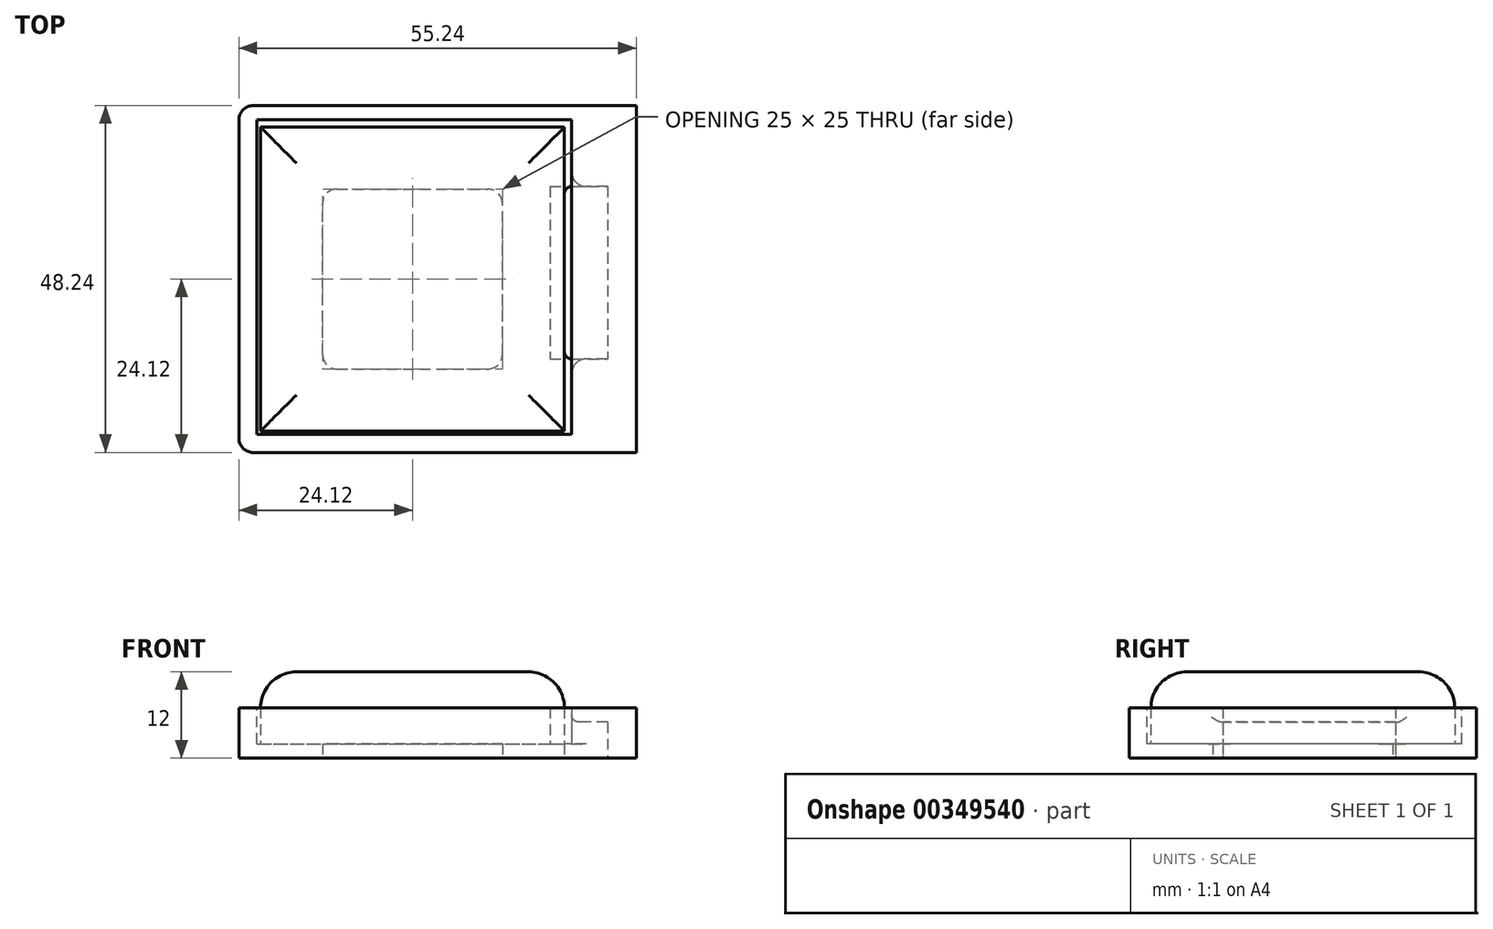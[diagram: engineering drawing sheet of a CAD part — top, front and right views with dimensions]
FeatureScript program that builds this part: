
annotation { "Feature Type Name" : "Feature", "Feature Type Description" : "" }
export const myFeature = defineFeature(function(context is Context, id is Id, definition is map)
    precondition{}
    {
        {
            var Q0;
            Q0=qCreatedBy(makeId("Top.planeOp"),FACE);
            var sketch = newSketch(context, id + "F0", { "sketchPlane" : qUnion([Q0])});
            skLineSegment(sketch, "E0.bottom", {"start": v(-21.12, 21.13) * mm, "end": v(21.13, 21.13) * mm});
            skLineSegment(sketch, "E0.top", {"start": v(-21.13, -21.12) * mm, "end": v(21.12, -21.12) * mm});
            skLineSegment(sketch, "E0.left", {"start": v(-21.12, 21.13) * mm, "end": v(-21.13, -21.12) * mm});
            skLineSegment(sketch, "E0.right", {"start": v(21.13, 21.13) * mm, "end": v(21.12, -21.12) * mm});
            skPoint(sketch, "E0.middle", {"position": v(0, 0) * mm});
            skSolve(sketch);
        }
        {
            var Q0;
            Q0 = qSketchRegion(id + "F0", true);
            extrude(context, id + "F1", {"entities" : qUnion([Q0]), "depth" : 10 * mm});
        }
        {
            var Q0;
            Q0=makeQuery(id+"F1.opExtrude","CAP_EDGE",EDGE,{"disambiguationData":[OSD([sQuery(id+"F0.wireOp",EDGE,"E0.left")])],"isStart":false});
            var Q1;
            Q1=makeQuery(id+"F1.opExtrude","CAP_EDGE",EDGE,{"disambiguationData":[OSD([sQuery(id+"F0.wireOp",EDGE,"E0.top")])],"isStart":false});
            var Q2;
            Q2=makeQuery(id+"F1.opExtrude","CAP_EDGE",EDGE,{"disambiguationData":[OSD([sQuery(id+"F0.wireOp",EDGE,"E0.right")])],"isStart":false});
            var Q3;
            Q3=makeQuery(id+"F1.opExtrude","CAP_EDGE",EDGE,{"disambiguationData":[OSD([sQuery(id+"F0.wireOp",EDGE,"E0.bottom")])],"isStart":false});
            fillet(context, id + "F2", {"entities" : qUnion([Q0, Q1, Q2, Q3]), "radius" : 5 * mm, "tangentPropagation" : true, "allowEdgeOverflow" : false});
        }
        {
            var Q0;
            Q0=makeQuery(id+"F1.opExtrude","SWEPT_FACE",FACE,{"disambiguationData":[OSD([sQuery(id+"F0.wireOp",EDGE,"E0.right")])]});
            var sketch = newSketch(context, id + "F3", { "sketchPlane" : qUnion([Q0])});
            skLineSegment(sketch, "E1.0", {"start": v(-21.12, 5) * mm, "end": v(-21.12, 0) * mm});
            skLineSegment(sketch, "E2.0", {"start": v(-11.12, 5) * mm, "end": v(-11.12, 0) * mm});
            skLineSegment(sketch, "E3.0", {"start": v(12.88, 5) * mm, "end": v(12.88, 0) * mm});
            skSolve(sketch);
        }
        {
            var Q0;
            Q0 = qSketchRegion(id + "F3", true);
            var Q1;
            {var subQ0=sQuery(id+"F3.wireOp",EDGE,"E2.0");Q1=makeQuery(id+"F3.imprint","IMPRINT",FACE,{"disambiguationData":[TD([[makeQuery(id+"F3.imprint","IMPRINT",EDGE,{"derivedFrom":subQ0}),1.0]])]});}
            extrude(context, id + "F4", {"entities" : qUnion([Q0, Q1]), "operationType" : NewBodyOperationType.REMOVE, "oppositeDirection" : true, "depth" : 2 * mm});
        }
        {
            var Q0;
            Q0=makeQuery(id+"F1.opExtrude","CAP_FACE",FACE,{"disambiguationData":[OSD([sQuery(id+"F0.wireOp",EDGE,"E0.bottom"),sQuery(id+"F0.wireOp",EDGE,"E0.top"),sQuery(id+"F0.wireOp",EDGE,"E0.left"),sQuery(id+"F0.wireOp",EDGE,"E0.right")])],"isStart":true});
            var sketch = newSketch(context, id + "F5", { "sketchPlane" : qUnion([Q0])});
            skLineSegment(sketch, "E4.0", {"start": v(-21.13, 21.12) * mm, "end": v(21.12, 21.12) * mm});
            skLineSegment(sketch, "E4.1", {"start": v(-21.12, -21.13) * mm, "end": v(21.13, -21.13) * mm});
            skLineSegment(sketch, "E4.2", {"start": v(21.13, -12.88) * mm, "end": v(21.12, 11.12) * mm});
            skLineSegment(sketch, "E4.3", {"start": v(21.12, 11.12) * mm, "end": v(21.12, 21.12) * mm});
            skLineSegment(sketch, "E4.4", {"start": v(21.13, -21.13) * mm, "end": v(21.13, -12.88) * mm});
            skLineSegment(sketch, "E5.0", {"start": v(-21.12, -21.13) * mm, "end": v(-21.13, 21.12) * mm});
            skLineSegment(sketch, "E6.0", {"start": v(19.13, -12.88) * mm, "end": v(21.13, -12.88) * mm});
            skLineSegment(sketch, "E6.1", {"start": v(19.12, 11.12) * mm, "end": v(21.12, 11.12) * mm});
            skLineSegment(sketch, "E7.0", {"start": v(22.13, -22.13) * mm, "end": v(22.13, -12.88) * mm});
            skLineSegment(sketch, "E7.1", {"start": v(22.13, 11.12) * mm, "end": v(22.12, 22.12) * mm});
            skLineSegment(sketch, "E7.2", {"start": v(-22.13, 22.12) * mm, "end": v(22.12, 22.12) * mm});
            skLineSegment(sketch, "E7.3", {"start": v(-22.12, -22.13) * mm, "end": v(-22.13, 22.12) * mm});
            skLineSegment(sketch, "E7.4", {"start": v(-22.12, -22.13) * mm, "end": v(22.13, -22.13) * mm});
            skLineSegment(sketch, "E8.0", {"start": v(24.13, -24.13) * mm, "end": v(24.13, -12.88) * mm});
            skLineSegment(sketch, "E8.1", {"start": v(24.12, 11.13) * mm, "end": v(24.12, 24.12) * mm});
            skLineSegment(sketch, "E8.2", {"start": v(-24.13, 24.12) * mm, "end": v(24.12, 24.12) * mm});
            skLineSegment(sketch, "E8.3", {"start": v(-24.12, -24.13) * mm, "end": v(-24.13, 24.12) * mm});
            skLineSegment(sketch, "E8.4", {"start": v(-24.12, -24.13) * mm, "end": v(24.13, -24.13) * mm});
            skLineSegment(sketch, "E9", {"start": v(24.13, -12.88) * mm, "end": v(22.13, -12.88) * mm});
            skLineSegment(sketch, "E10", {"start": v(24.12, 11.13) * mm, "end": v(22.13, 11.12) * mm});
            skSolve(sketch);
        }
        {
            var Q0;
            Q0=makeQuery(id+"F5.imprint","IMPRINT",FACE,{"disambiguationData":[TD([[makeQuery(id+"F5.imprint","IMPRINT",EDGE,{"derivedFrom":sQuery(id+"F5.wireOp",EDGE,"E4.0")}),-1.0]])]});
            var sketch = newSketch(context, id + "F6", { "sketchPlane" : qUnion([Q0])});
            skPoint(sketch, "E11.0", {"position": v(24.13, -24.13) * mm});
            skPoint(sketch, "E12.0", {"position": v(-24.13, 24.12) * mm});
            skLineSegment(sketch, "E13.bottom", {"start": v(24.13, -24.13) * mm, "end": v(-24.13, -24.13) * mm});
            skLineSegment(sketch, "E13.top", {"start": v(24.13, 24.12) * mm, "end": v(-24.13, 24.12) * mm});
            skLineSegment(sketch, "E13.left", {"start": v(24.13, -24.13) * mm, "end": v(24.13, 24.12) * mm});
            skLineSegment(sketch, "E13.right", {"start": v(-24.13, -24.13) * mm, "end": v(-24.13, 24.12) * mm});
            skSolve(sketch);
        }
        {
            var Q0;
            Q0 = qSketchRegion(id + "F6", true);
            extrude(context, id + "F7", {"entities" : qUnion([Q0]), "depth" : 2 * mm});
        }
        {
            var Q0;
            Q0=makeQuery(id+"F5.imprint","IMPRINT",FACE,{"disambiguationData":[TD([[makeQuery(id+"F5.imprint","IMPRINT",EDGE,{"derivedFrom":sQuery(id+"F5.wireOp",EDGE,"E7.0")}),-1.0]])]});
            extrude(context, id + "F8", {"entities" : qUnion([Q0]), "operationType" : NewBodyOperationType.ADD, "oppositeDirection" : true, "depth" : 5 * mm});
        }
        {
            var Q0;
            Q0=makeQuery(id+"F7.opExtrude","CAP_FACE",FACE,{"disambiguationData":[OSD([sQuery(id+"F6.wireOp",EDGE,"E13.bottom"),sQuery(id+"F6.wireOp",EDGE,"E13.top"),sQuery(id+"F6.wireOp",EDGE,"E13.left"),sQuery(id+"F6.wireOp",EDGE,"E13.right")])],"isStart":false});
            var sketch = newSketch(context, id + "F9", { "sketchPlane" : qUnion([Q0])});
            skLineSegment(sketch, "E14.0", {"start": v(21.13, -12.88) * mm, "end": v(21.12, 11.12) * mm});
            skLineSegment(sketch, "E15.0", {"start": v(19.13, -12.88) * mm, "end": v(24.13, -12.88) * mm});
            skLineSegment(sketch, "E16.0", {"start": v(19.13, 11.12) * mm, "end": v(24.13, 11.12) * mm});
            skLineSegment(sketch, "E17.0", {"start": v(24.13, -24.13) * mm, "end": v(24.13, 24.12) * mm});
            skSolve(sketch);
        }
        {
            var Q0;
            {var subQ0=sQuery(id+"F9.wireOp",EDGE,"E14.0");Q0=makeQuery(id+"F9.imprint","IMPRINT",FACE,{"disambiguationData":[TD([[makeQuery(id+"F9.imprint","IMPRINT",EDGE,{"derivedFrom":subQ0}),-1.0]])]});}
            extrude(context, id + "F10", {"entities" : qUnion([Q0]), "operationType" : NewBodyOperationType.REMOVE, "oppositeDirection" : true, "depth" : 25 * mm});
        }
        {
            var Q0;
            Q0=makeQuery(id+"F7.opExtrude","CAP_FACE",FACE,{"disambiguationData":[OSD([sQuery(id+"F6.wireOp",EDGE,"E13.bottom"),sQuery(id+"F6.wireOp",EDGE,"E13.top"),sQuery(id+"F6.wireOp",EDGE,"E13.left"),sQuery(id+"F6.wireOp",EDGE,"E13.right")])],"isStart":false});
            var sketch = newSketch(context, id + "F11", { "sketchPlane" : qUnion([Q0])});
            skLineSegment(sketch, "E18.0", {"start": v(21.12, 11.12) * mm, "end": v(24.13, 11.12) * mm});
            skLineSegment(sketch, "E19.0", {"start": v(21.13, -12.88) * mm, "end": v(21.12, 11.12) * mm});
            skLineSegment(sketch, "E20.0", {"start": v(21.13, -12.88) * mm, "end": v(24.13, -12.88) * mm});
            skLineSegment(sketch, "E21.0", {"start": v(24.13, 11.12) * mm, "end": v(24.13, 24.12) * mm});
            skLineSegment(sketch, "E22.0", {"start": v(24.13, 24.12) * mm, "end": v(-24.13, 24.12) * mm});
            skLineSegment(sketch, "E23.0", {"start": v(-24.13, -24.13) * mm, "end": v(-24.13, 24.12) * mm});
            skLineSegment(sketch, "E24.0", {"start": v(24.13, -24.13) * mm, "end": v(-24.13, -24.13) * mm});
            skLineSegment(sketch, "E25.0", {"start": v(24.13, -24.13) * mm, "end": v(24.13, -12.88) * mm});
            skLineSegment(sketch, "E26.MirrorCS", {"start": v(27.13, 11.12) * mm, "end": v(24.13, 11.12) * mm});
            skLineSegment(sketch, "E27.MirrorCS", {"start": v(27.13, -12.88) * mm, "end": v(27.13, 11.12) * mm});
            skLineSegment(sketch, "E28.MirrorCS", {"start": v(27.13, -12.88) * mm, "end": v(24.13, -12.88) * mm});
            skLineSegment(sketch, "E29.MirrorCS", {"start": v(24.13, -24.13) * mm, "end": v(72.38, -24.13) * mm});
            skLineSegment(sketch, "E30.MirrorCS", {"start": v(72.38, -24.13) * mm, "end": v(72.38, 24.12) * mm});
            skLineSegment(sketch, "E31.MirrorCS", {"start": v(24.13, 24.12) * mm, "end": v(72.38, 24.12) * mm});
            skLineSegment(sketch, "E32.0", {"start": v(15.13, -18.88) * mm, "end": v(24.13, -18.88) * mm});
            skLineSegment(sketch, "E32.1", {"start": v(15.12, 17.12) * mm, "end": v(24.13, 17.12) * mm});
            skLineSegment(sketch, "E32.2", {"start": v(33.13, 17.12) * mm, "end": v(24.13, 17.12) * mm});
            skLineSegment(sketch, "E32.3", {"start": v(15.13, -18.88) * mm, "end": v(15.12, 17.12) * mm});
            skLineSegment(sketch, "E32.4", {"start": v(33.13, -18.88) * mm, "end": v(33.13, 17.12) * mm});
            skLineSegment(sketch, "E32.5", {"start": v(33.13, -18.88) * mm, "end": v(24.13, -18.88) * mm});
            skLineSegment(sketch, "E33", {"start": v(24.13, 24.12) * mm, "end": v(24.13, -24.13) * mm});
            skLineSegment(sketch, "E34.MirrorCS", {"start": v(42.13, 24.12) * mm, "end": v(42.13, -24.13) * mm});
            skLineSegment(sketch, "E35.0", {"start": v(37.63, 24.12) * mm, "end": v(37.63, -24.13) * mm});
            skLineSegment(sketch, "E36.0", {"start": v(24.13, -14.13) * mm, "end": v(72.38, -14.13) * mm});
            skLineSegment(sketch, "E37.0", {"start": v(24.13, 14.12) * mm, "end": v(72.38, 14.12) * mm});
            skSolve(sketch);
        }
        {
            var Q0;
            {var subQ0=sQuery(id+"F11.wireOp",EDGE,"E32.2");Q0=makeQuery(id+"F11.imprint","IMPRINT",FACE,{"disambiguationData":[TD([[makeQuery(id+"F11.imprint","IMPRINT",EDGE,{"derivedFrom":subQ0}),-1.0]])]});}
            var Q1;
            {var subQ0=sQuery(id+"F11.wireOp",EDGE,"E34.MirrorCS");var subQ1=sQuery(id+"F11.wireOp",EDGE,"E31.MirrorCS");var subQ2=makeQuery(id+"F11.imprint","INTERSECT",VERTEX,{"derivedFrom":[subQ1,subQ0]});Q1=makeQuery(id+"F11.imprint","IMPRINT",FACE,{"disambiguationData":[TD([[makeQuery(id+"F11.imprint","IMPRINT",EDGE,{"disambiguationData":[TD([[subQ2,1.0]])],"derivedFrom":subQ1}),-1.0]])]});}
            var Q2;
            {var subQ0=sQuery(id+"F11.wireOp",EDGE,"E36.0");var subQ1=sQuery(id+"F11.wireOp",EDGE,"E32.4");var subQ2=makeQuery(id+"F11.imprint","INTERSECT",VERTEX,{"derivedFrom":[subQ1,subQ0]});Q2=makeQuery(id+"F11.imprint","IMPRINT",FACE,{"disambiguationData":[TD([[makeQuery(id+"F11.imprint","IMPRINT",EDGE,{"disambiguationData":[TD([[subQ2,-1.0]])],"derivedFrom":subQ1}),-1.0]])]});}
            var Q3;
            {var subQ0=sQuery(id+"F11.wireOp",EDGE,"E37.0");var subQ1=sQuery(id+"F11.wireOp",EDGE,"E34.MirrorCS");var subQ2=makeQuery(id+"F11.imprint","INTERSECT",VERTEX,{"derivedFrom":[subQ1,subQ0]});Q3=makeQuery(id+"F11.imprint","IMPRINT",FACE,{"disambiguationData":[TD([[makeQuery(id+"F11.imprint","IMPRINT",EDGE,{"disambiguationData":[TD([[subQ2,-1.0]])],"derivedFrom":subQ1}),-1.0]])]});}
            var Q4;
            {var subQ3=sQuery(id+"F11.wireOp",EDGE,"E32.5");Q4=makeQuery(id+"F11.imprint","IMPRINT",FACE,{"disambiguationData":[TD([[makeQuery(id+"F11.imprint","IMPRINT",EDGE,{"derivedFrom":subQ3}),1.0]])]});}
            var Q5;
            {var subQ0=sQuery(id+"F11.wireOp",EDGE,"E34.MirrorCS");var subQ1=sQuery(id+"F11.wireOp",EDGE,"E29.MirrorCS");var subQ2=makeQuery(id+"F11.imprint","INTERSECT",VERTEX,{"derivedFrom":[subQ1,subQ0]});Q5=makeQuery(id+"F11.imprint","IMPRINT",FACE,{"disambiguationData":[TD([[makeQuery(id+"F11.imprint","IMPRINT",EDGE,{"disambiguationData":[TD([[subQ2,1.0]])],"derivedFrom":subQ1}),1.0]])]});}
            var Q6;
            {var subQ7=sQuery(id+"F11.wireOp",EDGE,"E26.MirrorCS");Q6=makeQuery(id+"F11.imprint","IMPRINT",FACE,{"disambiguationData":[TD([[makeQuery(id+"F11.imprint","IMPRINT",EDGE,{"derivedFrom":subQ7}),-1.0]])]});}
            var Q7;
            {var subQ0=sQuery(id+"F11.wireOp",EDGE,"E32.5");Q7=makeQuery(id+"F11.imprint","IMPRINT",FACE,{"disambiguationData":[TD([[makeQuery(id+"F11.imprint","IMPRINT",EDGE,{"derivedFrom":subQ0}),-1.0]])]});}
            var Q8;
            {var subQ0=sQuery(id+"F11.wireOp",EDGE,"E32.2");Q8=makeQuery(id+"F11.imprint","IMPRINT",FACE,{"disambiguationData":[TD([[makeQuery(id+"F11.imprint","IMPRINT",EDGE,{"derivedFrom":subQ0}),1.0]])]});}
            extrude(context, id + "F12", {"entities" : qUnion([Q0, Q1, Q2, Q3, Q4, Q5, Q6, Q7, Q8]), "operationType" : NewBodyOperationType.ADD, "oppositeDirection" : true, "depth" : 4 * mm});
        }
        {
            var Q0;
            Q0=makeQuery(id+"F12.boolean.opBoolean","MERGE",FACE,{"derivedFrom":[makeQuery(id+"F8.boolean.opBoolean","MERGE",FACE,{"derivedFrom":[makeQuery(id+"F7.opExtrude","SWEPT_FACE",FACE,{"disambiguationData":[OSD([sQuery(id+"F6.wireOp",EDGE,"E13.top")])]}),makeQuery(id+"F8.opExtrude","SWEPT_FACE",FACE,{"disambiguationData":[OSD([sQuery(id+"F5.wireOp",EDGE,"E8.2")])]})]}),makeQuery(id+"F12.opExtrude","SWEPT_FACE",FACE,{"disambiguationData":[OSD([sQuery(id+"F11.wireOp",EDGE,"E31.MirrorCS")])]})]});
            var sketch = newSketch(context, id + "F13", { "sketchPlane" : qUnion([Q0])});
            skLineSegment(sketch, "E38.0", {"start": v(42.13, -2) * mm, "end": v(-24.13, -2) * mm});
            skLineSegment(sketch, "E39.0", {"start": v(-24.13, 5) * mm, "end": v(24.12, 5) * mm});
            skSolve(sketch);
        }
        {
            var Q0;
            Q0=makeQuery(id+"F12.opExtrude","CAP_FACE",FACE,{"disambiguationData":[OSD([sQuery(id+"F11.wireOp",EDGE,"E29.MirrorCS"),sQuery(id+"F11.wireOp",EDGE,"E31.MirrorCS"),sQuery(id+"F11.wireOp",EDGE,"E32.2"),sQuery(id+"F11.wireOp",EDGE,"E32.4"),sQuery(id+"F11.wireOp",EDGE,"E32.5"),sQuery(id+"F11.wireOp",EDGE,"E33"),sQuery(id+"F11.wireOp",EDGE,"E34.MirrorCS")])],"isStart":false});
            cPlane(context, id + "F14", {"entities" : qUnion([Q0]), "cplaneType" : CPlaneType.OFFSET, "offset" : 1 * mm, "width" : 150 * mm, "height" : 150 * mm});
        }
        {
            var Q0;
            Q0=qCreatedBy(id+"F14.planeOp",FACE);
            var sketch = newSketch(context, id + "F15", { "sketchPlane" : qUnion([Q0])});
            skLineSegment(sketch, "E40.0.0", {"start": v(42.13, -24.12) * mm, "end": v(42.13, 24.13) * mm});
            skLineSegment(sketch, "E40.0.1", {"start": v(42.13, 24.13) * mm, "end": v(24.13, 24.13) * mm});
            skLineSegment(sketch, "E40.0.2", {"start": v(24.13, 24.13) * mm, "end": v(24.13, 12.88) * mm});
            skLineSegment(sketch, "E40.0.3", {"start": v(24.13, 12.88) * mm, "end": v(27.13, 12.88) * mm});
            skLineSegment(sketch, "E40.0.4", {"start": v(27.13, 12.88) * mm, "end": v(27.13, -11.12) * mm});
            skLineSegment(sketch, "E40.0.5", {"start": v(27.13, -11.12) * mm, "end": v(24.12, -11.12) * mm});
            skLineSegment(sketch, "E40.0.6", {"start": v(24.13, -11.13) * mm, "end": v(24.13, -24.12) * mm});
            skLineSegment(sketch, "E40.0.7", {"start": v(24.13, -24.12) * mm, "end": v(42.13, -24.12) * mm});
            skSolve(sketch);
        }
        {
            var Q0;
            Q0=makeQuery(id+"F15.imprint","IMPRINT",FACE,{"disambiguationData":[TD([[makeQuery(id+"F15.imprint","IMPRINT",EDGE,{"derivedFrom":sQuery(id+"F15.wireOp",EDGE,"E40.0.0")}),1.0]])]});
            extrude(context, id + "F16", {"entities" : qUnion([Q0]), "operationType" : NewBodyOperationType.ADD, "depth" : 2 * mm});
        }
        {
            var Q0;
            Q0=makeQuery(id+"F12.boolean.opBoolean","MERGE",FACE,{"derivedFrom":[makeQuery(id+"F7.opExtrude","CAP_FACE",FACE,{"disambiguationData":[OSD([sQuery(id+"F6.wireOp",EDGE,"E13.bottom"),sQuery(id+"F6.wireOp",EDGE,"E13.top"),sQuery(id+"F6.wireOp",EDGE,"E13.left"),sQuery(id+"F6.wireOp",EDGE,"E13.right")])],"isStart":false}),makeQuery(id+"F12.opExtrude","CAP_FACE",FACE,{"disambiguationData":[OSD([sQuery(id+"F11.wireOp",EDGE,"E26.MirrorCS"),sQuery(id+"F11.wireOp",EDGE,"E27.MirrorCS"),sQuery(id+"F11.wireOp",EDGE,"E28.MirrorCS"),sQuery(id+"F11.wireOp",EDGE,"E29.MirrorCS"),sQuery(id+"F11.wireOp",EDGE,"E31.MirrorCS"),sQuery(id+"F11.wireOp",EDGE,"E33"),sQuery(id+"F11.wireOp",EDGE,"E34.MirrorCS")])],"isStart":true})]});
            var sketch = newSketch(context, id + "F17", { "sketchPlane" : qUnion([Q0])});
            skLineSegment(sketch, "E41.0.0", {"start": v(24.13, 11.12) * mm, "end": v(24.13, 24.12) * mm});
            skLineSegment(sketch, "E41.0.1", {"start": v(24.13, 24.12) * mm, "end": v(42.13, 24.12) * mm});
            skLineSegment(sketch, "E41.0.2", {"start": v(42.13, 24.12) * mm, "end": v(42.13, -24.13) * mm});
            skLineSegment(sketch, "E41.0.3", {"start": v(42.13, -24.13) * mm, "end": v(24.13, -24.13) * mm});
            skLineSegment(sketch, "E41.0.4", {"start": v(24.13, -24.13) * mm, "end": v(24.13, -12.88) * mm});
            skLineSegment(sketch, "E41.0.5", {"start": v(24.13, -12.88) * mm, "end": v(27.13, -12.88) * mm});
            skLineSegment(sketch, "E41.0.6", {"start": v(27.13, -12.88) * mm, "end": v(27.13, 11.12) * mm});
            skLineSegment(sketch, "E41.0.7", {"start": v(27.13, 11.12) * mm, "end": v(24.12, 11.12) * mm});
            skSolve(sketch);
        }
        {
            var Q0;
            Q0=makeQuery(id+"F16.boolean.opBoolean","MERGE",FACE,{"derivedFrom":[makeQuery(id+"F8.opExtrude","CAP_FACE",FACE,{"disambiguationData":[OSD([sQuery(id+"F5.wireOp",EDGE,"E7.0"),sQuery(id+"F5.wireOp",EDGE,"E7.1"),sQuery(id+"F5.wireOp",EDGE,"E7.2"),sQuery(id+"F5.wireOp",EDGE,"E7.3"),sQuery(id+"F5.wireOp",EDGE,"E7.4"),sQuery(id+"F5.wireOp",EDGE,"E8.0"),sQuery(id+"F5.wireOp",EDGE,"E8.1"),sQuery(id+"F5.wireOp",EDGE,"E8.2"),sQuery(id+"F5.wireOp",EDGE,"E8.3"),sQuery(id+"F5.wireOp",EDGE,"E8.4"),sQuery(id+"F5.wireOp",EDGE,"E9"),sQuery(id+"F5.wireOp",EDGE,"E10")])],"isStart":false}),makeQuery(id+"F16.opExtrude","CAP_FACE",FACE,{"disambiguationData":[OSD([sQuery(id+"F15.wireOp",EDGE,"E40.0.0"),sQuery(id+"F15.wireOp",EDGE,"E40.0.1"),sQuery(id+"F15.wireOp",EDGE,"E40.0.2"),sQuery(id+"F15.wireOp",EDGE,"E40.0.3"),sQuery(id+"F15.wireOp",EDGE,"E40.0.4"),sQuery(id+"F15.wireOp",EDGE,"E40.0.5"),sQuery(id+"F15.wireOp",EDGE,"E40.0.6"),sQuery(id+"F15.wireOp",EDGE,"E40.0.7")])],"isStart":false})]});
            var sketch = newSketch(context, id + "F18", { "sketchPlane" : qUnion([Q0])});
            skLineSegment(sketch, "E42.0", {"start": v(33.13, 18.88) * mm, "end": v(33.13, -17.12) * mm});
            skLineSegment(sketch, "E43.0", {"start": v(24.13, 14.13) * mm, "end": v(72.38, 14.13) * mm});
            skLineSegment(sketch, "E44.0", {"start": v(24.13, -14.12) * mm, "end": v(72.38, -14.12) * mm});
            skPoint(sketch, "E45", {"position": v(33.13, 14.13) * mm});
            skPoint(sketch, "E46", {"position": v(33.13, -14.12) * mm});
            skSolve(sketch);
        }
        {
            var Q0;
            Q0=makeQuery(id+"F13.imprint","IMPRINT",FACE,{"disambiguationData":[TD([[makeQuery(id+"F13.imprint","IMPRINT",EDGE,{"derivedFrom":sQuery(id+"F13.wireOp",EDGE,"E38.0")}),-1.0]])]});
            var sketch = newSketch(context, id + "F19", { "sketchPlane" : qUnion([Q0])});
            skLineSegment(sketch, "E47.0", {"start": v(42.13, 2) * mm, "end": v(42.13, -2) * mm});
            skLineSegment(sketch, "E48.0", {"start": v(24.13, 2) * mm, "end": v(42.13, 2) * mm});
            skLineSegment(sketch, "E49.0", {"start": v(37.13, 2) * mm, "end": v(37.13, -2) * mm});
            skPoint(sketch, "E50", {"position": v(37.13, 2) * mm});
            skSolve(sketch);
        }
        {
            var Q0;
            Q0=makeQuery(id+"F12.boolean.opBoolean","MERGE",FACE,{"derivedFrom":[makeQuery(id+"F7.opExtrude","CAP_FACE",FACE,{"disambiguationData":[OSD([sQuery(id+"F6.wireOp",EDGE,"E13.bottom"),sQuery(id+"F6.wireOp",EDGE,"E13.top"),sQuery(id+"F6.wireOp",EDGE,"E13.left"),sQuery(id+"F6.wireOp",EDGE,"E13.right")])],"isStart":false}),makeQuery(id+"F12.opExtrude","CAP_FACE",FACE,{"disambiguationData":[OSD([sQuery(id+"F11.wireOp",EDGE,"E26.MirrorCS"),sQuery(id+"F11.wireOp",EDGE,"E27.MirrorCS"),sQuery(id+"F11.wireOp",EDGE,"E28.MirrorCS"),sQuery(id+"F11.wireOp",EDGE,"E29.MirrorCS"),sQuery(id+"F11.wireOp",EDGE,"E31.MirrorCS"),sQuery(id+"F11.wireOp",EDGE,"E33"),sQuery(id+"F11.wireOp",EDGE,"E34.MirrorCS")])],"isStart":true})]});
            var sketch = newSketch(context, id + "F20", { "sketchPlane" : qUnion([Q0])});
            skLineSegment(sketch, "E51.bottom", {"start": v(-12.5, 12.5) * mm, "end": v(12.5, 12.5) * mm});
            skLineSegment(sketch, "E51.top", {"start": v(-12.5, -12.5) * mm, "end": v(12.5, -12.5) * mm});
            skLineSegment(sketch, "E51.left", {"start": v(-12.5, 12.5) * mm, "end": v(-12.5, -12.5) * mm});
            skLineSegment(sketch, "E51.right", {"start": v(12.5, 12.5) * mm, "end": v(12.5, -12.5) * mm});
            skPoint(sketch, "E51.middle", {"position": v(0, 0) * mm});
            skSolve(sketch);
        }
        {
            var Q0;
            Q0=makeQuery(id+"F20.imprint","IMPRINT",FACE,{"disambiguationData":[TD([[makeQuery(id+"F20.imprint","IMPRINT",EDGE,{"derivedFrom":sQuery(id+"F20.wireOp",EDGE,"E51.bottom")}),-1.0]])]});
            var Q1;
            Q1=makeQuery(id+"F7.opExtrude","CAP_FACE",FACE,{"disambiguationData":[OSD([sQuery(id+"F6.wireOp",EDGE,"E13.bottom"),sQuery(id+"F6.wireOp",EDGE,"E13.top"),sQuery(id+"F6.wireOp",EDGE,"E13.left"),sQuery(id+"F6.wireOp",EDGE,"E13.right")])],"isStart":true});
            extrude(context, id + "F21", {"entities" : qUnion([Q0]), "operationType" : NewBodyOperationType.REMOVE, "endBound" : BoundingType.UP_TO_SURFACE, "oppositeDirection" : true, "endBoundEntityFace" : qUnion([Q1]), "depth" : 25 * mm});
        }
        {
            var Q0;
            Q0=makeQuery(id+"F16.boolean.opBoolean","MERGE",FACE,{"derivedFrom":[makeQuery(id+"F8.opExtrude","CAP_FACE",FACE,{"disambiguationData":[OSD([sQuery(id+"F5.wireOp",EDGE,"E7.0"),sQuery(id+"F5.wireOp",EDGE,"E7.1"),sQuery(id+"F5.wireOp",EDGE,"E7.2"),sQuery(id+"F5.wireOp",EDGE,"E7.3"),sQuery(id+"F5.wireOp",EDGE,"E7.4"),sQuery(id+"F5.wireOp",EDGE,"E8.0"),sQuery(id+"F5.wireOp",EDGE,"E8.1"),sQuery(id+"F5.wireOp",EDGE,"E8.2"),sQuery(id+"F5.wireOp",EDGE,"E8.3"),sQuery(id+"F5.wireOp",EDGE,"E8.4"),sQuery(id+"F5.wireOp",EDGE,"E9"),sQuery(id+"F5.wireOp",EDGE,"E10")])],"isStart":false}),makeQuery(id+"F16.opExtrude","CAP_FACE",FACE,{"disambiguationData":[OSD([sQuery(id+"F15.wireOp",EDGE,"E40.0.0"),sQuery(id+"F15.wireOp",EDGE,"E40.0.1"),sQuery(id+"F15.wireOp",EDGE,"E40.0.2"),sQuery(id+"F15.wireOp",EDGE,"E40.0.3"),sQuery(id+"F15.wireOp",EDGE,"E40.0.4"),sQuery(id+"F15.wireOp",EDGE,"E40.0.5"),sQuery(id+"F15.wireOp",EDGE,"E40.0.6"),sQuery(id+"F15.wireOp",EDGE,"E40.0.7")])],"isStart":false})]});
            var sketch = newSketch(context, id + "F22", { "sketchPlane" : qUnion([Q0])});
            skLineSegment(sketch, "E52.0", {"start": v(42.13, -24.12) * mm, "end": v(42.13, 24.13) * mm});
            skLineSegment(sketch, "E53.0", {"start": v(-24.12, 24.13) * mm, "end": v(42.13, 24.13) * mm});
            skLineSegment(sketch, "E54.0", {"start": v(-24.13, -24.12) * mm, "end": v(42.13, -24.12) * mm});
            skLineSegment(sketch, "E55.0", {"start": v(22.13, -11.12) * mm, "end": v(22.12, -24.12) * mm});
            skLineSegment(sketch, "E56.0", {"start": v(27.13, -11.13) * mm, "end": v(22.13, -11.12) * mm});
            skLineSegment(sketch, "E57.0", {"start": v(27.13, 12.88) * mm, "end": v(27.13, -11.12) * mm});
            skLineSegment(sketch, "E58.0", {"start": v(22.13, 24.13) * mm, "end": v(22.13, 22.13) * mm});
            skLineSegment(sketch, "E59.0", {"start": v(27.13, 12.88) * mm, "end": v(22.13, 12.88) * mm});
            skPoint(sketch, "E60.orphan", {"position": v(22.12, -22.12) * mm});
            skSolve(sketch);
        }
        {
            var Q0;
            {var subQ1=sQuery(id+"F22.wireOp",EDGE,"E52.0");Q0=makeQuery(id+"F22.imprint","IMPRINT",FACE,{"disambiguationData":[TD([[makeQuery(id+"F22.imprint","IMPRINT",EDGE,{"derivedFrom":subQ1}),1.0]])]});}
            var Q1;
            Q1=makeQuery(id+"F12.boolean.opBoolean","MERGE",FACE,{"derivedFrom":[makeQuery(id+"F7.opExtrude","CAP_FACE",FACE,{"disambiguationData":[OSD([sQuery(id+"F6.wireOp",EDGE,"E13.bottom"),sQuery(id+"F6.wireOp",EDGE,"E13.top"),sQuery(id+"F6.wireOp",EDGE,"E13.left"),sQuery(id+"F6.wireOp",EDGE,"E13.right")])],"isStart":false}),makeQuery(id+"F12.opExtrude","CAP_FACE",FACE,{"disambiguationData":[OSD([sQuery(id+"F11.wireOp",EDGE,"E26.MirrorCS"),sQuery(id+"F11.wireOp",EDGE,"E27.MirrorCS"),sQuery(id+"F11.wireOp",EDGE,"E28.MirrorCS"),sQuery(id+"F11.wireOp",EDGE,"E29.MirrorCS"),sQuery(id+"F11.wireOp",EDGE,"E31.MirrorCS"),sQuery(id+"F11.wireOp",EDGE,"E33"),sQuery(id+"F11.wireOp",EDGE,"E34.MirrorCS")])],"isStart":true})]});
            extrude(context, id + "F23", {"entities" : qUnion([Q0]), "operationType" : NewBodyOperationType.ADD, "endBound" : BoundingType.UP_TO_SURFACE, "oppositeDirection" : true, "endBoundEntityFace" : qUnion([Q1]), "depth" : 25 * mm});
        }
        {
            var Q0;
            Q0=makeQuery(id+"F16.boolean.opBoolean","MERGE",FACE,{"derivedFrom":[makeQuery(id+"F8.opExtrude","CAP_FACE",FACE,{"disambiguationData":[OSD([sQuery(id+"F5.wireOp",EDGE,"E7.0"),sQuery(id+"F5.wireOp",EDGE,"E7.1"),sQuery(id+"F5.wireOp",EDGE,"E7.2"),sQuery(id+"F5.wireOp",EDGE,"E7.3"),sQuery(id+"F5.wireOp",EDGE,"E7.4"),sQuery(id+"F5.wireOp",EDGE,"E8.0"),sQuery(id+"F5.wireOp",EDGE,"E8.1"),sQuery(id+"F5.wireOp",EDGE,"E8.2"),sQuery(id+"F5.wireOp",EDGE,"E8.3"),sQuery(id+"F5.wireOp",EDGE,"E8.4"),sQuery(id+"F5.wireOp",EDGE,"E9"),sQuery(id+"F5.wireOp",EDGE,"E10")])],"isStart":false}),makeQuery(id+"F16.opExtrude","CAP_FACE",FACE,{"disambiguationData":[OSD([sQuery(id+"F15.wireOp",EDGE,"E40.0.0"),sQuery(id+"F15.wireOp",EDGE,"E40.0.1"),sQuery(id+"F15.wireOp",EDGE,"E40.0.2"),sQuery(id+"F15.wireOp",EDGE,"E40.0.3"),sQuery(id+"F15.wireOp",EDGE,"E40.0.4"),sQuery(id+"F15.wireOp",EDGE,"E40.0.5"),sQuery(id+"F15.wireOp",EDGE,"E40.0.6"),sQuery(id+"F15.wireOp",EDGE,"E40.0.7")])],"isStart":false})]});
            var sketch = newSketch(context, id + "F24", { "sketchPlane" : qUnion([Q0])});
            skLineSegment(sketch, "E61.0", {"start": v(42.13, -24.12) * mm, "end": v(42.13, 24.13) * mm});
            skLineSegment(sketch, "E62.0", {"start": v(-24.12, 24.13) * mm, "end": v(42.13, 24.13) * mm});
            skLineSegment(sketch, "E63.0", {"start": v(-24.13, -24.12) * mm, "end": v(42.13, -24.12) * mm});
            skLineSegment(sketch, "E64.0", {"start": v(31.13, -24.12) * mm, "end": v(31.13, 24.13) * mm});
            skSolve(sketch);
        }
        {
            var Q0;
            {var subQ0=sQuery(id+"F24.wireOp",EDGE,"E61.0");Q0=makeQuery(id+"F24.imprint","IMPRINT",FACE,{"disambiguationData":[TD([[makeQuery(id+"F24.imprint","IMPRINT",EDGE,{"derivedFrom":subQ0}),1.0]])]});}
            extrude(context, id + "F25", {"entities" : qUnion([Q0]), "operationType" : NewBodyOperationType.REMOVE, "oppositeDirection" : true, "depth" : 25 * mm});
        }
        {
            var Q0;
            Q0=makeQuery(id+"F25.boolean.opBoolean","COPY",EDGE,{"derivedFrom":makeQuery(id+"F25.opExtrude","SWEPT_EDGE",EDGE,{"disambiguationData":[OSD([sQuery(id+"F24.wireOp",EDGE,"E62.0"),sQuery(id+"F24.wireOp",EDGE,"E64.0")])]})});
            var Q1;
            Q1=makeQuery(id+"F8.boolean.opBoolean","MERGE",EDGE,{"derivedFrom":[makeQuery(id+"F7.opExtrude","SWEPT_EDGE",EDGE,{"disambiguationData":[OSD([sQuery(id+"F6.wireOp",EDGE,"E13.bottom"),sQuery(id+"F6.wireOp",EDGE,"E13.right")])]}),makeQuery(id+"F8.opExtrude","SWEPT_EDGE",EDGE,{"disambiguationData":[OSD([sQuery(id+"F5.wireOp",EDGE,"E8.3"),sQuery(id+"F5.wireOp",EDGE,"E8.4")])]})]});
            var Q2;
            Q2=makeQuery(id+"F8.boolean.opBoolean","MERGE",EDGE,{"derivedFrom":[makeQuery(id+"F7.opExtrude","SWEPT_EDGE",EDGE,{"disambiguationData":[OSD([sQuery(id+"F6.wireOp",EDGE,"E13.top"),sQuery(id+"F6.wireOp",EDGE,"E13.right")])]}),makeQuery(id+"F8.opExtrude","SWEPT_EDGE",EDGE,{"disambiguationData":[OSD([sQuery(id+"F5.wireOp",EDGE,"E8.2"),sQuery(id+"F5.wireOp",EDGE,"E8.3")])]})]});
            var Q3;
            Q3=makeQuery(id+"F25.boolean.opBoolean","COPY",EDGE,{"derivedFrom":makeQuery(id+"F25.opExtrude","SWEPT_EDGE",EDGE,{"disambiguationData":[OSD([sQuery(id+"F24.wireOp",EDGE,"E63.0"),sQuery(id+"F24.wireOp",EDGE,"E64.0")])]})});
            var Q4;
            Q4=makeQuery(id+"F8.opExtrude","SWEPT_EDGE",EDGE,{"disambiguationData":[OSD([sQuery(id+"F5.wireOp",EDGE,"E7.1"),sQuery(id+"F5.wireOp",EDGE,"E10")])]});
            var Q5;
            Q5=makeQuery(id+"F8.opExtrude","SWEPT_EDGE",EDGE,{"disambiguationData":[OSD([sQuery(id+"F5.wireOp",EDGE,"E7.0"),sQuery(id+"F5.wireOp",EDGE,"E9")])]});
            var Q6;
            Q6=makeQuery(id+"F21.boolean.opBoolean","COPY",EDGE,{"derivedFrom":makeQuery(id+"F21.opExtrude","SWEPT_EDGE",EDGE,{"disambiguationData":[OSD([sQuery(id+"F20.wireOp",EDGE,"E51.top"),sQuery(id+"F20.wireOp",EDGE,"E51.right")])]})});
            var Q7;
            Q7=makeQuery(id+"F21.boolean.opBoolean","COPY",EDGE,{"derivedFrom":makeQuery(id+"F21.opExtrude","SWEPT_EDGE",EDGE,{"disambiguationData":[OSD([sQuery(id+"F20.wireOp",EDGE,"E51.top"),sQuery(id+"F20.wireOp",EDGE,"E51.left")])]})});
            var Q8;
            Q8=makeQuery(id+"F21.boolean.opBoolean","COPY",EDGE,{"derivedFrom":makeQuery(id+"F21.opExtrude","SWEPT_EDGE",EDGE,{"disambiguationData":[OSD([sQuery(id+"F20.wireOp",EDGE,"E51.bottom"),sQuery(id+"F20.wireOp",EDGE,"E51.left")])]})});
            var Q9;
            Q9=makeQuery(id+"F21.boolean.opBoolean","COPY",EDGE,{"derivedFrom":makeQuery(id+"F21.opExtrude","SWEPT_EDGE",EDGE,{"disambiguationData":[OSD([sQuery(id+"F20.wireOp",EDGE,"E51.bottom"),sQuery(id+"F20.wireOp",EDGE,"E51.right")])]})});
            fillet(context, id + "F26", {"entities" : qUnion([Q0, Q1, Q2, Q3, Q4, Q5, Q6, Q7, Q8, Q9]), "radius" : 2 * mm, "tangentPropagation" : true, "allowEdgeOverflow" : false});
        }
        {
            var Q0;
            Q0=makeQuery(id+"F16.boolean.opBoolean","MERGE",FACE,{"derivedFrom":[makeQuery(id+"F8.opExtrude","CAP_FACE",FACE,{"disambiguationData":[OSD([sQuery(id+"F5.wireOp",EDGE,"E7.0"),sQuery(id+"F5.wireOp",EDGE,"E7.1"),sQuery(id+"F5.wireOp",EDGE,"E7.2"),sQuery(id+"F5.wireOp",EDGE,"E7.3"),sQuery(id+"F5.wireOp",EDGE,"E7.4"),sQuery(id+"F5.wireOp",EDGE,"E8.0"),sQuery(id+"F5.wireOp",EDGE,"E8.1"),sQuery(id+"F5.wireOp",EDGE,"E8.2"),sQuery(id+"F5.wireOp",EDGE,"E8.3"),sQuery(id+"F5.wireOp",EDGE,"E8.4"),sQuery(id+"F5.wireOp",EDGE,"E9"),sQuery(id+"F5.wireOp",EDGE,"E10")])],"isStart":false}),makeQuery(id+"F16.opExtrude","CAP_FACE",FACE,{"disambiguationData":[OSD([sQuery(id+"F15.wireOp",EDGE,"E40.0.0"),sQuery(id+"F15.wireOp",EDGE,"E40.0.1"),sQuery(id+"F15.wireOp",EDGE,"E40.0.2"),sQuery(id+"F15.wireOp",EDGE,"E40.0.3"),sQuery(id+"F15.wireOp",EDGE,"E40.0.4"),sQuery(id+"F15.wireOp",EDGE,"E40.0.5"),sQuery(id+"F15.wireOp",EDGE,"E40.0.6"),sQuery(id+"F15.wireOp",EDGE,"E40.0.7")])],"isStart":false})]});
            var sketch = newSketch(context, id + "F27", { "sketchPlane" : qUnion([Q0])});
            skLineSegment(sketch, "E65.0.0", {"start": v(-22.13, -24.12) * mm, "end": v(29.13, -24.12) * mm});
            skArc(sketch, "E65.0.1", {"start": v(29.13, -24.12) * mm, "mid": v(30.54, -23.54) * mm, "end": v(31.13, -22.12) * mm});
            skLineSegment(sketch, "E65.0.2", {"start": v(31.13, -22.12) * mm, "end": v(31.13, 22.13) * mm});
            skArc(sketch, "E65.0.3", {"start": v(31.13, 22.13) * mm, "mid": v(30.54, 23.54) * mm, "end": v(29.13, 24.13) * mm});
            skLineSegment(sketch, "E65.0.4", {"start": v(29.13, 24.13) * mm, "end": v(-22.13, 24.13) * mm});
            skArc(sketch, "E65.0.5", {"start": v(-22.13, 24.13) * mm, "mid": v(-23.54, 23.54) * mm, "end": v(-24.13, 22.13) * mm});
            skLineSegment(sketch, "E65.0.6", {"start": v(-24.12, 22.13) * mm, "end": v(-24.13, -22.12) * mm});
            skArc(sketch, "E65.0.7", {"start": v(-24.13, -22.12) * mm, "mid": v(-23.54, -23.54) * mm, "end": v(-22.13, -24.12) * mm});
            skLineSegment(sketch, "E66.0", {"start": v(22.13, -13.13) * mm, "end": v(22.12, -22.12) * mm});
            skArc(sketch, "E67.0", {"start": v(24.13, -11.13) * mm, "mid": v(22.71, -11.71) * mm, "end": v(22.12, -13.13) * mm});
            skLineSegment(sketch, "E68.0", {"start": v(27.13, -11.13) * mm, "end": v(24.13, -11.13) * mm});
            skLineSegment(sketch, "E69.0", {"start": v(27.13, 12.88) * mm, "end": v(27.13, -11.12) * mm});
            skLineSegment(sketch, "E70.0", {"start": v(27.13, 12.88) * mm, "end": v(24.13, 12.88) * mm});
            skArc(sketch, "E71.0", {"start": v(22.13, 14.88) * mm, "mid": v(22.71, 13.46) * mm, "end": v(24.13, 12.88) * mm});
            skLineSegment(sketch, "E72.0", {"start": v(22.13, 22.13) * mm, "end": v(22.13, 14.88) * mm});
            skLineSegment(sketch, "E73", {"start": v(22.13, -13.13) * mm, "end": v(22.13, 14.88) * mm});
            skSolve(sketch);
        }
        {
            var Q0;
            Q0=makeQuery(id+"F27.imprint","IMPRINT",FACE,{"disambiguationData":[TD([[makeQuery(id+"F27.imprint","IMPRINT",EDGE,{"derivedFrom":sQuery(id+"F27.wireOp",EDGE,"E67.0")}),-1.0]])]});
            extrude(context, id + "F28", {"entities" : qUnion([Q0]), "operationType" : NewBodyOperationType.ADD, "oppositeDirection" : true, "depth" : 2 * mm});
        }
        {
            var Q0;
            Q0=makeQuery(id+"F28.opExtrude","CAP_EDGE",EDGE,{"disambiguationData":[OSD([sQuery(id+"F27.wireOp",EDGE,"E73")])],"isStart":false});
            fillet(context, id + "F29", {"entities" : qUnion([Q0]), "radius" : 1 * mm, "tangentPropagation" : true, "allowEdgeOverflow" : false});
        }
        {
            var Q0;
            Q0=makeQuery(id+"F10.boolean.opBoolean","COPY",EDGE,{"derivedFrom":makeQuery(id+"F10.opExtrude","SWEPT_EDGE",EDGE,{"disambiguationData":[OSD([sQuery(id+"F9.wireOp",EDGE,"E14.0"),sQuery(id+"F9.wireOp",EDGE,"E16.0")])]})});
            var Q1;
            Q1=makeQuery(id+"F10.boolean.opBoolean","COPY",EDGE,{"derivedFrom":makeQuery(id+"F10.opExtrude","SWEPT_EDGE",EDGE,{"disambiguationData":[OSD([sQuery(id+"F9.wireOp",EDGE,"E14.0"),sQuery(id+"F9.wireOp",EDGE,"E15.0")])]})});
            fillet(context, id + "F30", {"entities" : qUnion([Q0, Q1]), "radius" : 1 * mm, "tangentPropagation" : true, "allowEdgeOverflow" : false});
        }
        {
            var Q0;
            Q0=makeQuery(id+"F28.boolean.opBoolean","MERGE",FACE,{"derivedFrom":[makeQuery(id+"F16.boolean.opBoolean","MERGE",FACE,{"derivedFrom":[makeQuery(id+"F8.opExtrude","CAP_FACE",FACE,{"disambiguationData":[OSD([sQuery(id+"F5.wireOp",EDGE,"E7.0"),sQuery(id+"F5.wireOp",EDGE,"E7.1"),sQuery(id+"F5.wireOp",EDGE,"E7.2"),sQuery(id+"F5.wireOp",EDGE,"E7.3"),sQuery(id+"F5.wireOp",EDGE,"E7.4"),sQuery(id+"F5.wireOp",EDGE,"E8.0"),sQuery(id+"F5.wireOp",EDGE,"E8.1"),sQuery(id+"F5.wireOp",EDGE,"E8.2"),sQuery(id+"F5.wireOp",EDGE,"E8.3"),sQuery(id+"F5.wireOp",EDGE,"E8.4"),sQuery(id+"F5.wireOp",EDGE,"E9"),sQuery(id+"F5.wireOp",EDGE,"E10")])],"isStart":false}),makeQuery(id+"F16.opExtrude","CAP_FACE",FACE,{"disambiguationData":[OSD([sQuery(id+"F15.wireOp",EDGE,"E40.0.0"),sQuery(id+"F15.wireOp",EDGE,"E40.0.1"),sQuery(id+"F15.wireOp",EDGE,"E40.0.2"),sQuery(id+"F15.wireOp",EDGE,"E40.0.3"),sQuery(id+"F15.wireOp",EDGE,"E40.0.4"),sQuery(id+"F15.wireOp",EDGE,"E40.0.5"),sQuery(id+"F15.wireOp",EDGE,"E40.0.6"),sQuery(id+"F15.wireOp",EDGE,"E40.0.7")])],"isStart":false})]}),makeQuery(id+"F28.opExtrude","CAP_FACE",FACE,{"disambiguationData":[OSD([sQuery(id+"F27.wireOp",EDGE,"E67.0"),sQuery(id+"F27.wireOp",EDGE,"E68.0"),sQuery(id+"F27.wireOp",EDGE,"E69.0"),sQuery(id+"F27.wireOp",EDGE,"E70.0"),sQuery(id+"F27.wireOp",EDGE,"E71.0"),sQuery(id+"F27.wireOp",EDGE,"E73")])],"isStart":true})]});
            var sketch = newSketch(context, id + "F31", { "sketchPlane" : qUnion([Q0])});
            skLineSegment(sketch, "E74.0.0", {"start": v(-22.13, -24.12) * mm, "end": v(29.13, -24.12) * mm});
            skArc(sketch, "E74.0.1", {"start": v(29.13, -24.12) * mm, "mid": v(30.54, -23.54) * mm, "end": v(31.13, -22.12) * mm});
            skLineSegment(sketch, "E74.0.2", {"start": v(31.13, -22.12) * mm, "end": v(31.13, 22.13) * mm});
            skArc(sketch, "E74.0.3", {"start": v(31.13, 22.13) * mm, "mid": v(30.54, 23.54) * mm, "end": v(29.13, 24.13) * mm});
            skLineSegment(sketch, "E74.0.4", {"start": v(29.13, 24.13) * mm, "end": v(-22.13, 24.13) * mm});
            skArc(sketch, "E74.0.5", {"start": v(-22.13, 24.13) * mm, "mid": v(-23.54, 23.54) * mm, "end": v(-24.13, 22.13) * mm});
            skLineSegment(sketch, "E74.0.6", {"start": v(-24.12, 22.13) * mm, "end": v(-24.13, -22.12) * mm});
            skArc(sketch, "E74.0.7", {"start": v(-24.13, -22.12) * mm, "mid": v(-23.54, -23.54) * mm, "end": v(-22.13, -24.12) * mm});
            skLineSegment(sketch, "E75.0", {"start": v(-22.13, -22.12) * mm, "end": v(22.12, -22.12) * mm});
            skLineSegment(sketch, "E76.0", {"start": v(-22.12, 22.13) * mm, "end": v(-22.13, -22.12) * mm});
            skLineSegment(sketch, "E77.0", {"start": v(-21.62, 22.13) * mm, "end": v(-21.63, -22.12) * mm});
            skLineSegment(sketch, "E78.0", {"start": v(-22.13, -21.62) * mm, "end": v(22.12, -21.62) * mm});
            skLineSegment(sketch, "E79.0", {"start": v(-22.12, 22.13) * mm, "end": v(22.13, 22.13) * mm});
            skLineSegment(sketch, "E80.0", {"start": v(22.13, 22.13) * mm, "end": v(22.12, -22.12) * mm});
            skSolve(sketch);
        }
        {
            var Q0;
            {var subQ0=sQuery(id+"F31.wireOp",EDGE,"E79.0");var subQ1=sQuery(id+"F31.wireOp",EDGE,"E76.0");var subQ2=makeQuery(id+"F31.imprint","INTERSECT",VERTEX,{"derivedFrom":[subQ1,subQ0]});Q0=makeQuery(id+"F31.imprint","IMPRINT",FACE,{"disambiguationData":[TD([[makeQuery(id+"F31.imprint","IMPRINT",EDGE,{"disambiguationData":[TD([[subQ2,-1.0]])],"derivedFrom":subQ1}),1.0]])]});}
            var Q1;
            {var subQ0=sQuery(id+"F31.wireOp",EDGE,"E80.0");var subQ1=sQuery(id+"F31.wireOp",EDGE,"E75.0");var subQ2=makeQuery(id+"F31.imprint","INTERSECT",VERTEX,{"derivedFrom":[subQ1,subQ0]});Q1=makeQuery(id+"F31.imprint","IMPRINT",FACE,{"disambiguationData":[TD([[makeQuery(id+"F31.imprint","IMPRINT",EDGE,{"disambiguationData":[TD([[subQ2,1.0]])],"derivedFrom":subQ1}),1.0]])]});}
            var Q2;
            {var subQ0=sQuery(id+"F31.wireOp",EDGE,"E76.0");var subQ1=sQuery(id+"F31.wireOp",EDGE,"E75.0");var subQ2=makeQuery(id+"F31.imprint","INTERSECT",VERTEX,{"derivedFrom":[subQ1,subQ0]});Q2=makeQuery(id+"F31.imprint","IMPRINT",FACE,{"disambiguationData":[TD([[makeQuery(id+"F31.imprint","IMPRINT",EDGE,{"disambiguationData":[TD([[subQ2,-1.0]])],"derivedFrom":subQ1}),1.0]])]});}
            var Q3;
            Q3=makeQuery(id+"F7.opExtrude","CAP_FACE",FACE,{"disambiguationData":[OSD([sQuery(id+"F6.wireOp",EDGE,"E13.bottom"),sQuery(id+"F6.wireOp",EDGE,"E13.top"),sQuery(id+"F6.wireOp",EDGE,"E13.left"),sQuery(id+"F6.wireOp",EDGE,"E13.right")])],"isStart":true});
            extrude(context, id + "F32", {"entities" : qUnion([Q0, Q1, Q2]), "operationType" : NewBodyOperationType.ADD, "endBound" : BoundingType.UP_TO_SURFACE, "oppositeDirection" : true, "endBoundEntityFace" : qUnion([Q3]), "depth" : 25 * mm});
        }
    });
